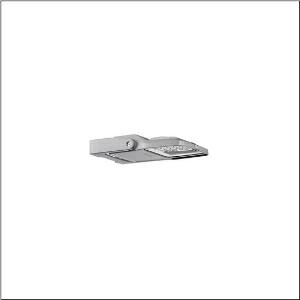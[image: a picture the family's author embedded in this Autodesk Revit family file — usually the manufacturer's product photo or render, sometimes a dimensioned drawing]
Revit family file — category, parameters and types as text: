
# Revit family: floodlight_fl_21_iq_micro___pl52_5xa7762a2d2a_5d06
name_source: partatom
category: Lighting Fixtures
units: mm (PartAtom-declared; Revit-internal decimal feet)

## family parameters
Cut with Voids When Loaded = No
Host = Face
Light Source = No
Part Type = Normal
Room Calculation Point = No
Round Connector Dimension = Use Diameter
Shared = No

## types (1)
- --- (1 x LED, 2890 lm, 23.1 W, 3000K)
    Apparent Load = 23 VA
    CIE Flux Codes = 26 60 98 100 100
    Color Rendering = 70
    Color Temperature = 3000K
    Default Elevation = 1800 mm
    Description = Floodlight FL 21 iQ micro, floodlight, primary light control with lens, of PMMA, primary optical cover: protective disc, of toughened safety glass, transparent, light distribution: PL52, light emission: direct distribution, installation type: surface-mounted, LED, High Power LED, rated luminous flux: 2.890lm, luminous efficacy: 125lm/W, light colour: 730, colour temperature: 3000K, control: Auto-Match, Temp-Guard, Night-Set, Smart-Wire, Desk-Remote (wireless, voltage-free reading and setting of iQ features in the workshop via application-optimized NFC function/RFID function), optimised constant luminous flux control (CLO 2.0), Street-Remote, with terminal, 6-pole, mains connection: 220..240V, AC, 50/60Hz, start of lifetime: 23W, end of service life: 24W, reduction: 11W, luminaire housing, of diecast aluminium, powder-coated, Siteco® metallic grey (DB 702S), corrosivity category C5 mid according to DIN EN ISO 12944, sealing non-destructively replaceable, design bracket, of diecast aluminium, powder-coated, Siteco® metallic grey (DB 702S), protection rating (complete): IP66, insulation class (complete): insulation class II (safety insulation), certification: CE, ENEC, VDE, protection symbol: D, impact resistance: IK07, permissible operating ambient temperature: -40..+40°C, permissible operating ambient temperature for outdoor applications: -40..+50°C, standard: DIN EN 12944, LABS conformity tested according to VDMA 24364:2018-05, packaging unit: 1 piece

Light Distribution: PL52
    Height = 65 mm
    Lamp = 1 x LED
    Lamp Light Flux = 2890 lm
    Lamp Power = 23.1 W
    Lamp count = 1
    Length = 312 mm
    Luminous efficacy = 125 lm/W
    Manufacturer = Siteco
    ModVariant = No
    Model = 5XA7762A2D2A
    Mounting Place = Wall
    Mounting Type = Surface mounted
    Number of Poles = 1
    OnlyDefault = Yes
    Power Factor = 1
    Product Name = Floodlight FL 21 iQ micro | PL52
    Product group = floodlight | wall mounted
    ProductGroupID = 2001
    Protection Class = Protection class II
    Protection Degree = IP 66
    RLX_Detail_Level = 1
    RLX_Emergency_Light_Flux = 0 lm
    RLX_Emergency_Type = 0
    RLX_Emergency_Type_DB = No
    RlxData = <blob elided: 97577 chars, md5=789152b1>
    Socket = socket
    Standby Power = 0 W
    System Light Flux = 2890 lm
    System Power = 23 W
    Type Comments = factory setting: luminous flux: 100 % | dim-lin: 254 | 455 mA
    Type Image = l_1006878.jpg
    URL = http://relux.com
    VarID = @adj_129067
    Voltage = 0 V
    Weight = 0.00 kg
    Width = 230 mm

## geometry (parser evidence)
native form markers: Blend x4, Sweep x14
no freeform markers — native parametric forms only
